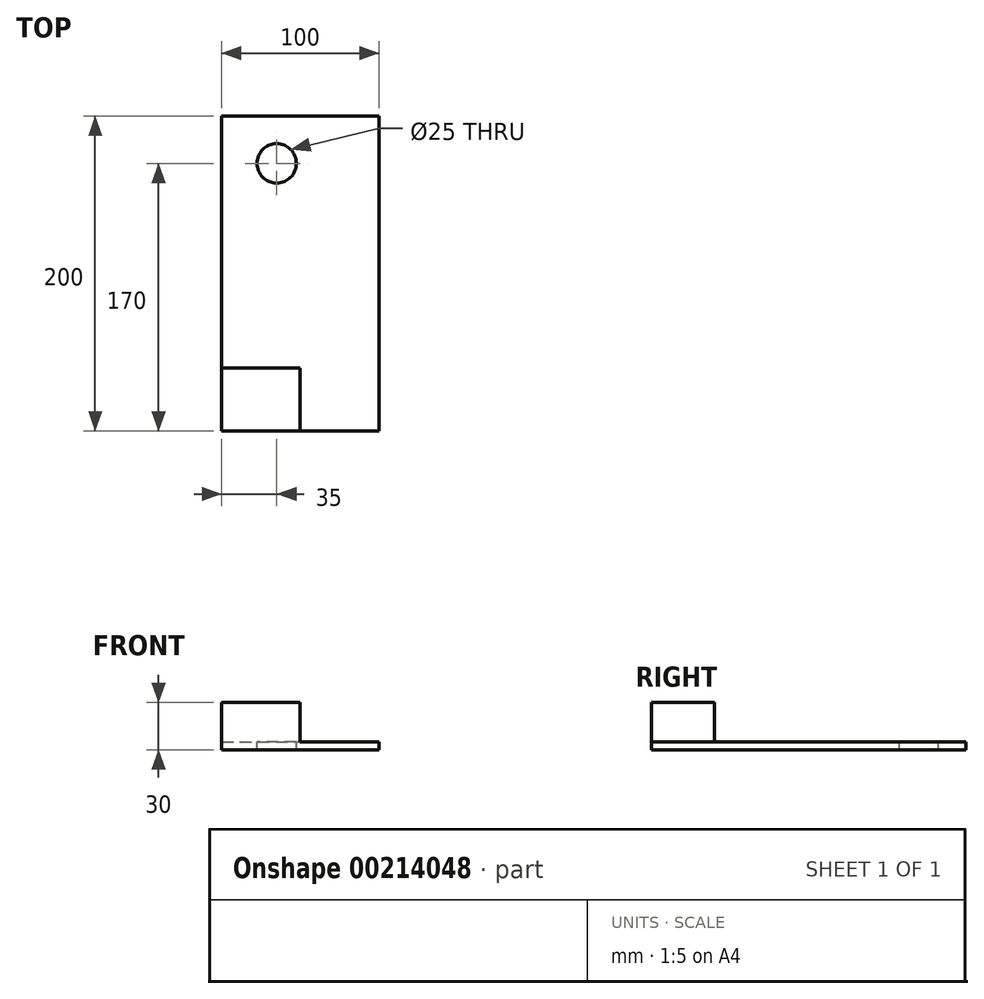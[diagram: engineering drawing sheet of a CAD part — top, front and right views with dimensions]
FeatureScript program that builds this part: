
annotation { "Feature Type Name" : "Feature", "Feature Type Description" : "" }
export const myFeature = defineFeature(function(context is Context, id is Id, definition is map)
    precondition{}
    {
        {
            var Q0;
            Q0=qCreatedBy(makeId("Top.planeOp"),FACE);
            var sketch = newSketch(context, id + "F0", { "sketchPlane" : qUnion([Q0])});
            skLineSegment(sketch, "E0.bottom", {"start": v(50, 100) * mm, "end": v(-50, 100) * mm});
            skLineSegment(sketch, "E0.top", {"start": v(50, -100) * mm, "end": v(-50, -100) * mm});
            skLineSegment(sketch, "E0.left", {"start": v(50, 100) * mm, "end": v(50, -100) * mm});
            skLineSegment(sketch, "E0.right", {"start": v(-50, 100) * mm, "end": v(-50, -100) * mm});
            skPoint(sketch, "E0.middle", {"position": v(0, 0) * mm});
            skSolve(sketch);
        }
        {
            var Q0;
            Q0=makeQuery(id+"F0.imprint","IMPRINT",FACE,{"disambiguationData":[TD([[makeQuery(id+"F0.imprint","IMPRINT",EDGE,{"derivedFrom":sQuery(id+"F0.wireOp",EDGE,"E0.bottom")}),1.0]])]});
            extrude(context, id + "F1", {"entities" : qUnion([Q0]), "depth" : 5 * mm});
        }
        {
            var Q0;
            Q0=makeQuery(id+"F1.opExtrude","CAP_FACE",FACE,{"disambiguationData":[OSD([sQuery(id+"F0.wireOp",EDGE,"E0.bottom"),sQuery(id+"F0.wireOp",EDGE,"E0.top"),sQuery(id+"F0.wireOp",EDGE,"E0.left"),sQuery(id+"F0.wireOp",EDGE,"E0.right")])],"isStart":false});
            var sketch = newSketch(context, id + "F2", { "sketchPlane" : qUnion([Q0])});
            skLineSegment(sketch, "E1.bottom", {"start": v(-50, -100) * mm, "end": v(0, -100) * mm});
            skLineSegment(sketch, "E1.top", {"start": v(-50, -60) * mm, "end": v(0, -60) * mm});
            skLineSegment(sketch, "E1.left", {"start": v(-50, -100) * mm, "end": v(-50, -60) * mm});
            skLineSegment(sketch, "E1.right", {"start": v(0, -100) * mm, "end": v(0, -60) * mm});
            skSolve(sketch);
        }
        {
            var Q0;
            Q0=makeQuery(id+"F2.imprint","IMPRINT",FACE,{"disambiguationData":[TD([[makeQuery(id+"F2.imprint","IMPRINT",EDGE,{"derivedFrom":sQuery(id+"F2.wireOp",EDGE,"E1.bottom")}),-1.0]])]});
            extrude(context, id + "F3", {"entities" : qUnion([Q0]), "operationType" : NewBodyOperationType.ADD, "depth" : 25 * mm});
        }
        {
            var Q0;
            Q0=makeQuery(id+"F1.opExtrude","CAP_FACE",FACE,{"disambiguationData":[OSD([sQuery(id+"F0.wireOp",EDGE,"E0.bottom"),sQuery(id+"F0.wireOp",EDGE,"E0.top"),sQuery(id+"F0.wireOp",EDGE,"E0.left"),sQuery(id+"F0.wireOp",EDGE,"E0.right")])],"isStart":false});
            var sketch = newSketch(context, id + "F4", { "sketchPlane" : qUnion([Q0])});
            skPoint(sketch, "E2", {"position": v(-15, 70) * mm});
            skSolve(sketch);
        }
        {
            var Q0;
            Q0=sQuery(id+"F4.wireOp",VERTEX,"E2");
            var Q1;
            Q1=makeQuery(id+"F1.opExtrude","SWEPT_BODY",BODY,{"disambiguationData":[OSD([sQuery(id+"F0.wireOp",EDGE,"E0.bottom"),sQuery(id+"F0.wireOp",EDGE,"E0.top"),sQuery(id+"F0.wireOp",EDGE,"E0.left"),sQuery(id+"F0.wireOp",EDGE,"E0.right")])]});
            hole(context, id + "F5", {"style" : HoleStyle.SIMPLE, "endStyle" : HoleEndStyle.THROUGH, "standardTappedOrClearance" : lookupTablePath({ "standard" : "ISO", "size" : "25", "type" : "Drilled" }), "standardBlindInLast" : lookupTablePath({ "standard" : "ISO", "size" : "25", "type" : "Drilled" }), "holeDiameter" : 25 * mm, "locations" : qUnion([Q0]), "scope" : qUnion([Q1]), "isTappedThrough" : true});
        }
    });
